# Revit family: KORF_ANR
name_source: partatom
category: Оборудование
units: mm (PartAtom-declared; Revit-internal decimal feet)

## family parameters
Всегда вертикально = Да
Заголовок OmniClass = Climate Control (HVAC)
На основе рабочей плоскости = Нет
Номер OmniClass = 23.75.00.00
Общий = Нет
При загрузке вырезать с полостями = Нет
Размер круглого соединителя = Использовать диаметр
Сохранять ориентацию аннотаций = Нет
Тип детали = Нормальный
Точка принадлежности помещению = Нет

## types (5) — shared parameters
ADSK_Группирование = 10
ADSK_Единица измерения = шт.
ADSK_Завод-изготовитель = KORF
ADSK_Количество = 1
ADSK_Напряжение = 380 В
c2 = 150 мм
zero-valued in all types: Отметка по умолчанию

## per-type parameters (varying)
| type | A | ADSK_Марка | ADSK_Масса_Текст | ADSK_Наименование | ADSK_Наименование краткое | ADSK_Номинальная мощность | ADSK_Частота вращения вентилятора | ADSK_Частота вращения двигателя | B | H | a1 | a2 | b1 | b2 | c1 | h |
| ANR6 L/K2U/P2/F4/N1.2/V1.0.P56.R-7,5x15/H1/Z2/P2 | 4450 мм | ANR6 | 621,6 | Приточная установка ANR6 L/K2U/P2/F4/N1.2/V1.0.P56.R-7,5x15/H1/Z2/P2 | ANR6 L/K2U/P2/F4/N1.2/V1.0.P56.R-7,5x15/H1/Z2/P2 [Напольная] | 7500 Вт | 1440 | 1440 | 1100 мм | 1100 мм | 1068 мм | 1068 мм | 568 мм | 568 мм | 325 мм | 120 мм |
| ANR8 L/K2U/P2/F4/N1.2/V1.0.P63.R-7,5x15/H1/Z2/P2 | 4450 мм | ANR8 | 787 | Приточная установка ANR8 L/K2U/P2/F4/N1.2/V1.0.P63.R-7,5x15/H1/Z2/P2 | ANR8 L/K2U/P2/F4/N1.2/V1.0.P63.R-7,5x15/H1/Z2/P2 [Напольная] | 7500 Вт | 1440 | 1440 | 1320 мм | 1440 мм | 1268 мм | 1268 мм | 568 мм | 568 мм | 325 мм | 120 мм |
| UTR 80-50 V1.40-4x30.R | 3730 мм | UTR 80-50 | 293 | Приточная установка UTR 80-50 V1.40-4x30.R [Напольная] | UTR 80-50 V1.40-4x30.R [Напольная] | 4000 Вт | 2850 | 2850 | 1010 мм | 720 мм | 840 мм | 840 мм | 540 мм | 540 мм | 328 мм | 50 мм |
| UTR 90-50 V1.40-4x30.R | 3770 мм | UTR 90-50 | 323 | Приточная установка UTR 90-50 V1.40-4x30.R [Напольная] | UTR 90-50 V1.40-4x30.R [Напольная] | 4000 Вт | 2850 | 2850 | 1125 мм | 740 мм | 960 мм | 960 мм | 560 мм | 560 мм | 340 мм | 50 мм |
| ANR6 P/K2U/P2/F4/V1.0.P45.R-7,5x30/H1/Z2/P2 | 3875 мм | ANR6 | 506 | Приточная установка ANR6 P/K2U/P2/F4/V1.0.P45.R-7,5x30/H1/Z2/P2 [Напольная] | ANR6 P/K2U/P2/F4/V1.0.P45.R-7,5x30/H1/Z2/P2 [Напольная] | 7500 Вт | 2890 | 2890 | 1100 мм | 1100 мм | 1068 мм | 1068 мм | 568 мм | 568 мм | 325 мм | 120 мм |
